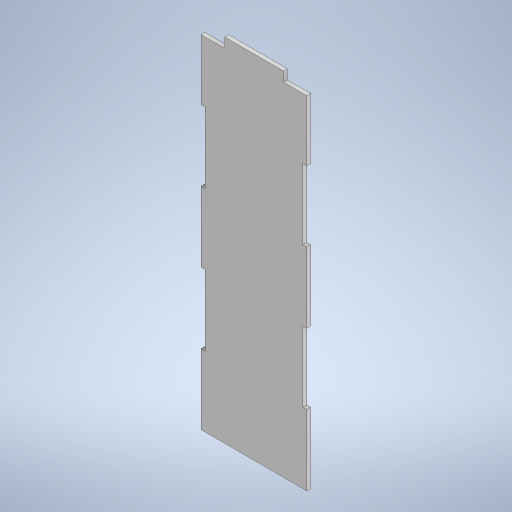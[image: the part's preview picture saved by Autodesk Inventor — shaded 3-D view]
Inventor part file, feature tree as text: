
AUTODESK INVENTOR PART (.ipt)
format: ipt  version: 2023 (Build 270158000, 158)  size: 264,192 bytes
history: native  units: mm
features: extrude x3, sketch x3
ambient origin geometry x8: Origin, YZ Plane, XZ Plane, XY Plane, X Axis, Y Axis, Z Axis, Center Point
bodies: Solid1 (feature_tree)
feature tree (6):
  extrude  "Extrusion1"  Depth=180.0mm
  extrude  "Extrusion2"  Depth=12.0mm
  extrude  "Extrusion3"  Depth=5.0mm
  sketch  "Sketch1"  dims[d0=54.0mm d1=180.0mm]
  sketch  "Sketch2"  dims[d2=2.0mm d3=0.0mm d4=12.0mm]
  sketch  "Sketch3"  dims[d5=12.0mm d6=5.0mm d7=2.0mm d8=0.0mm d10=36.0mm d11=36.0mm d12=2.0mm d13=2.0mm d14=36.0mm d15=36.0mm d16=2.0mm d17=0.0mm]
